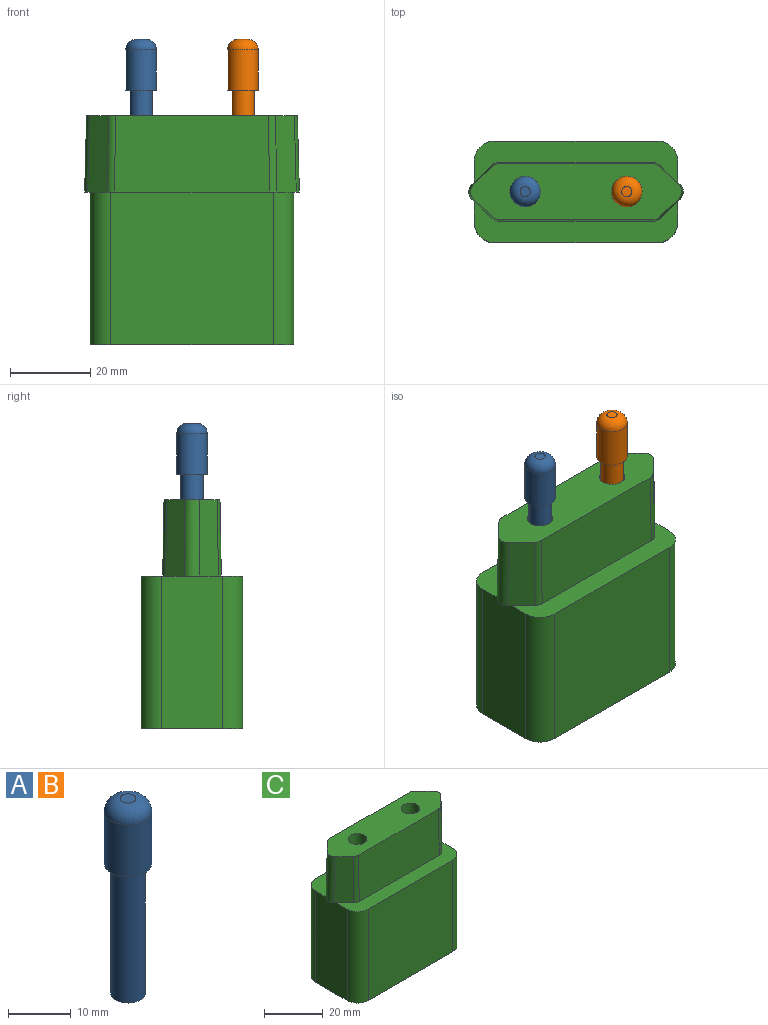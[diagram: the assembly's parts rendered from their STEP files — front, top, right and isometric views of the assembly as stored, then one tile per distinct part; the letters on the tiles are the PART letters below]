
ASSEMBLY  parts=3 mates=2
PART A: 6 faces, bbox 7.6x7.6x38.1 mm
  f0: cylinder r=2.79mm len=25.4mm, axis (0,0,-1), area 445.9mm2, adj f1,f3
  f1: plane 5.59x5.59mm, normal (0,0,-1), area 24.5mm2, adj f0
  f2: cylinder r=3.81mm len=10.16mm, axis (0,0,1), area 243.2mm2, adj f3,f5
  f3: plane 7.62x7.62mm, normal (0,0,-1), area 21.1mm2, adj f0,f2
  f4: plane 2.54x2.54mm, normal (0,0,1), area 5.1mm2, adj f5
  f5: torus R=1.27mm, axis (0,0,1), area 72.4mm2, adj f2,f4
PART B: same geometry as A
PART C: 40 faces, bbox 53.6x25.4x57.2 mm
  f0: plane 50.8x25.4mm, normal (0,0,-1), area 1113.3mm2, adj f4,f5,f6,f7,f8,f9,f10,f11
  f1: plane 52.67x13.97mm, normal (0,0,1), area 598.6mm2, adj f13,f14,f15,f16,f17,f18,f20,f21
  f2: plane 50.81x10.27mm, normal (0,0,1), area 287.4mm2, adj f4,f5,f7,f8,f11,f13,f17,f18
  f3: plane 50.81x10.27mm, normal (0,0,1), area 287.4mm2, adj f5,f6,f7,f9,f10,f14,f15,f16
  f4: plane 40.64x38.1mm, normal (0,1,0), area 1548.4mm2, adj f0,f2,f8,f11
  f5: plane 38.1x15.24mm, normal (-1,0,0), area 580.6mm2, adj f0,f2,f3,f8,f9,f12
  f6: plane 40.64x38.1mm, normal (0,-1,0), area 1548.4mm2, adj f0,f3,f9,f10
  f7: plane 38.1x15.24mm, normal (1,0,0), area 580.6mm2, adj f0,f2,f3,f10,f11,f19
  f8: cylinder r=5.08mm len=38.1mm, axis (0,0,1), area 304mm2, adj f0,f2,f4,f5
  f9: cylinder r=5.08mm len=38.1mm, axis (0,0,-1), area 304mm2, adj f0,f3,f5,f6
  f10: cylinder r=5.08mm len=38.1mm, axis (0,0,1), area 304mm2, adj f0,f3,f6,f7
  f11: cylinder r=5.08mm len=38.1mm, axis (0,0,-1), area 304mm2, adj f0,f2,f4,f7
  f12: plane 4.88x1.41mm, normal (0,0,-1), area 4.7mm2, adj f5,f13,f14,f20
  f13: plane 19.05x5.11mm, normal (-0.69,0.72,0.02), area 126.8mm2, adj f1,f2,f12,f20,f25
  f14: plane 19.05x5.11mm, normal (-0.69,-0.72,0.02), area 126.8mm2, adj f1,f3,f12,f20,f22
  f15: plane 38.6x19.05mm, normal (0,-1,0.02), area 732.8mm2, adj f1,f3,f22,f23
  f16: plane 19.05x5.11mm, normal (0.69,-0.72,0.02), area 126.8mm2, adj f1,f3,f19,f21,f23
  f17: plane 19.05x5.11mm, normal (0.69,0.72,0.02), area 126.8mm2, adj f1,f2,f19,f21,f24
  f18: plane 38.6x19.05mm, normal (0,1,0.02), area 732.8mm2, adj f1,f2,f24,f25
  f19: plane 4.88x1.41mm, normal (0,0,-1), area 4.7mm2, adj f7,f16,f17,f21
  f20: cylinder r=2.54mm len=19.09mm, axis (-0.03,0,-1), area 78mm2, adj f1,f12,f13,f14
  f21: cylinder r=2.54mm len=19.09mm, axis (0.03,0,-1), area 78mm2, adj f1,f16,f17,f19
  f22: cylinder r=2.54mm len=19.05mm, axis (-0.01,-0.02,-1), area 37mm2, adj f1,f3,f14,f15
  f23: cylinder r=2.54mm len=19.05mm, axis (0.01,-0.02,-1), area 37mm2, adj f1,f3,f15,f16
  f24: cylinder r=2.54mm len=19.05mm, axis (0.01,0.02,-1), area 37mm2, adj f1,f2,f17,f18
  f25: cylinder r=2.54mm len=19.05mm, axis (-0.01,0.02,-1), area 37mm2, adj f1,f2,f13,f18
  f26: plane 6.35x6.35mm, normal (0,0,1), area 31.7mm2, adj f27
  f27: cylinder r=3.17mm len=19.05mm, axis (0,0,1), area 380mm2, adj f1,f26
  f28: plane 6.35x6.35mm, normal (0,0,1), area 31.7mm2, adj f29
  f29: cylinder r=3.17mm len=19.05mm, axis (0,0,1), area 380mm2, adj f1,f28
  f30: plane 15.24x12.7mm, normal (0,1,0), area 193.5mm2, adj f0,f31,f33,f34
  f31: plane 12.7x5.08mm, normal (1,0,0), area 64.5mm2, adj f0,f30,f32,f34
  f32: plane 15.24x12.7mm, normal (0,-1,0), area 193.5mm2, adj f0,f31,f33,f34
  f33: plane 12.7x5.08mm, normal (-1,0,0), area 64.5mm2, adj f0,f30,f32,f34
  f34: plane 15.24x5.08mm, normal (0,0,-1), area 77.4mm2, adj f30,f31,f32,f33
  f35: plane 15.24x12.7mm, normal (0,1,0), area 193.5mm2, adj f0,f36,f38,f39
  f36: plane 12.7x5.08mm, normal (1,0,0), area 64.5mm2, adj f0,f35,f37,f39
  f37: plane 15.24x12.7mm, normal (0,-1,0), area 193.5mm2, adj f0,f36,f38,f39
  f38: plane 12.7x5.08mm, normal (-1,0,0), area 64.5mm2, adj f0,f35,f37,f39
  f39: plane 15.24x5.08mm, normal (0,0,-1), area 77.4mm2, adj f35,f36,f37,f38
PLACE A t=(11.36,11.74,54.5)mm
PLACE B t=(36.76,11.74,54.5)mm
PLACE C t=(24.06,11.74,16.4)mm
MATE fastened B.f0 <-> C.f27  axis (0,0,-1) through (36.76,11.74,54.5)mm
MATE fastened A.f0 <-> C.f29  axis (0,0,-1) through (11.36,11.74,54.5)mm
